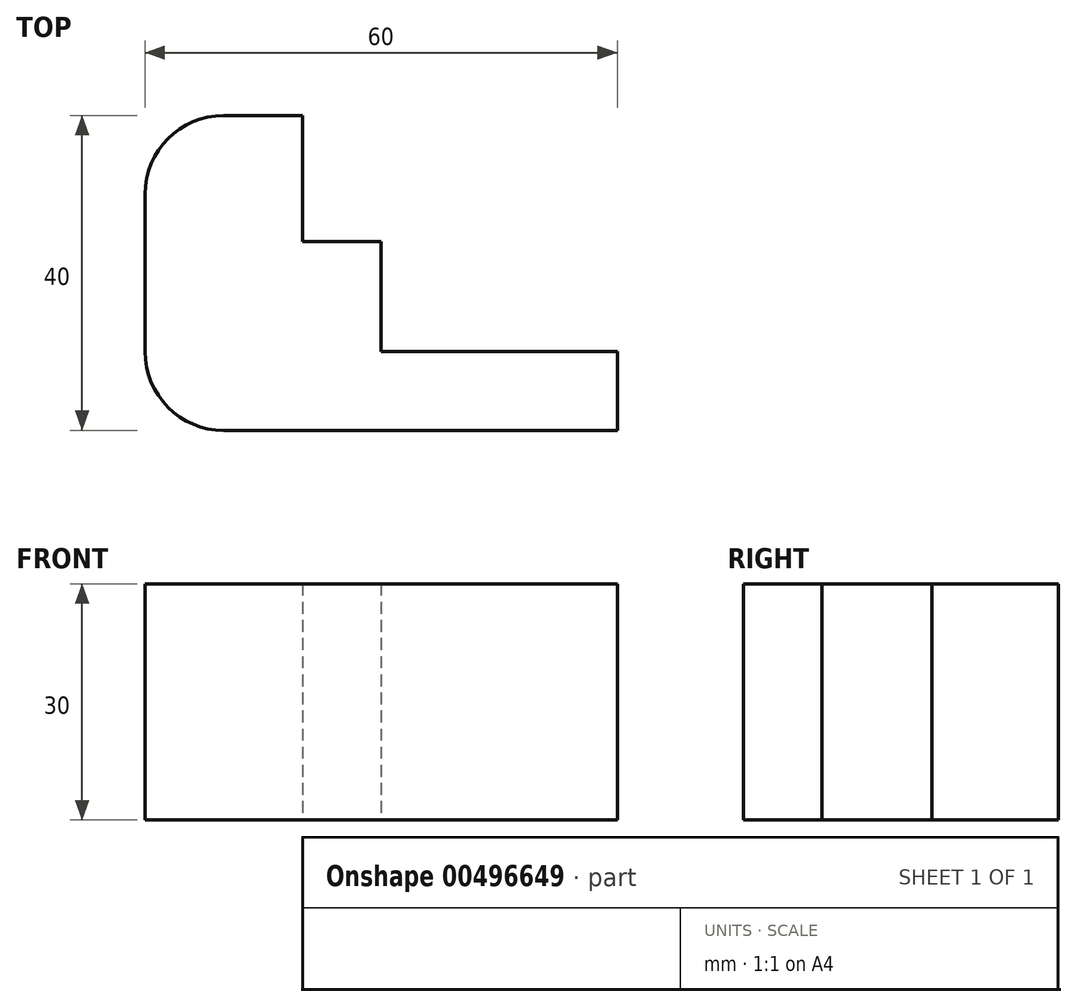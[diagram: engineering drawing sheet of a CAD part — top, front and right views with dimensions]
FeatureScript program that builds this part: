
annotation { "Feature Type Name" : "Feature", "Feature Type Description" : "" }
export const myFeature = defineFeature(function(context is Context, id is Id, definition is map)
    precondition{}
    {
        {
            var Q0;
            Q0=qCreatedBy(makeId("Top.planeOp"),FACE);
            var sketch = newSketch(context, id + "F0", { "sketchPlane" : qUnion([Q0])});
            skLineSegment(sketch, "E0", {"start": v(10, 0) * mm, "end": v(60, 0) * mm});
            skLineSegment(sketch, "E1", {"start": v(0, 10) * mm, "end": v(0, 30) * mm});
            skLineSegment(sketch, "E2", {"start": v(60, 0) * mm, "end": v(60, 10) * mm});
            skLineSegment(sketch, "E3", {"start": v(60, 10) * mm, "end": v(30, 10) * mm});
            skLineSegment(sketch, "E4", {"start": v(30, 10) * mm, "end": v(30, 24) * mm});
            skLineSegment(sketch, "E5", {"start": v(10, 40) * mm, "end": v(20, 40) * mm});
            skLineSegment(sketch, "E6", {"start": v(20, 40) * mm, "end": v(20, 24) * mm});
            skLineSegment(sketch, "E7", {"start": v(20, 24) * mm, "end": v(30, 24) * mm});
            skPoint(sketch, "E8.visualSharp", {"position": v(0, 40) * mm});
            skArc(sketch, "E8.filletArc", {"start": v(10, 40) * mm, "mid": v(2.93, 37.07) * mm, "end": v(0, 30) * mm});
            skPoint(sketch, "E9.visualSharp", {"position": v(0, 0) * mm});
            skArc(sketch, "E9.filletArc", {"start": v(0, 10) * mm, "mid": v(2.93, 2.93) * mm, "end": v(10, 0) * mm});
            skSolve(sketch);
        }
        {
            var Q0;
            Q0 = qSketchRegion(id + "F0", true);
            extrude(context, id + "F1", {"entities" : qUnion([Q0]), "depth" : 30 * mm, "offsetDistance" : 25 * mm});
        }
    });
